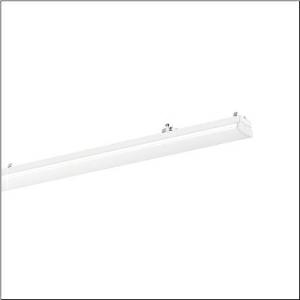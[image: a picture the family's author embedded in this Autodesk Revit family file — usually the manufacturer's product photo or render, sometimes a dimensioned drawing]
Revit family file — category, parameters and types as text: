
# Revit family: licross_r__21_recessed_opal_mo_52te1dvn465g_d803
name_source: partatom
category: Lighting Fixtures
units: mm (PartAtom-declared; Revit-internal decimal feet)

## family parameters
Cut with Voids When Loaded = No
Host = Face
Light Source = No
Part Type = Normal
Room Calculation Point = No
Round Connector Dimension = Use Diameter
Shared = No

## types (1)
- --- (1 x LED, 6500 lm, 37.7 W, 4000K)
    Apparent Load = 38 VA
    CIE Flux Codes = 44 73 91 87 100
    Color Rendering = 80
    Color Temperature = 4000K
    Default Elevation = 1800 mm
    Description = Licross® 21 recessed opal MO, luminaire insert, of sheet steel, galvanised, coil coated, white, length: 1.500mm, width: 66mm, height: 67mm, LED rated luminous flux: 6.500lm, light colour: 840, control gear: DALI 2, CLO, with plug, 5-pole, with phase selection, mains connection: 220..240V, AC, 50/60Hz, start of lifetime: 38W, end of service life: 45W, internal wiring halogen-free, primary optical cover: cover, of PMMA, light emission: direct with ceiling illumination distribution, primary light characteristic: symmetric, protection rating (complete): IP54, insulation class (complete): insulation class I (protective earthing), certification: CE, ENEC, VDE, UKCA, protection symbol: D if used in an environment with non-conductive dust loads with corresponding accessories, impact resistance: IK06, permissible ambient temperature for indoor applications: -25..+40°C, corresponds to IFS (International Featured Standards) requirements for safety and quality in the food industry, reducing of maximum allowable ambient temperature of 5°C with ceiling mounting, LABS conformity tested according to VDMA 24364:2018-05, packaging unit: 1 piece
    Height = 83 mm
    Lamp = 1 x LED
    Lamp Light Flux = 6500 lm
    Lamp Power = 37.7 W
    Lamp count = 1
    Length = 1500 mm
    Luminous efficacy = 172 lm/W
    Manufacturer = Siteco
    ModVariant = No
    Model = 52TE1DVN465G
    Mounting Place = Ceiling
    Mounting Type = Pendant
    Number of Poles = 1
    OnlyDefault = Yes
    Power Factor = 1
    Product Name = Licross® 21 recessed opal MO
    Product group = luminaire insert | ceiling pendant
    ProductGroupID = 902
    Protection Class = Protection class I
    Protection Degree = IP 54
    RLX_Detail_Level = 1
    RLX_Emergency_Light_Flux = 0 lm
    RLX_Emergency_Type = 0
    RLX_Emergency_Type_DB = No
    RlxData = <blob elided: 27321 chars, md5=6a89600c>
    Socket = socket
    Standby Power = 0 W
    System Light Flux = 6500 lm
    System Power = 38 W
    Type Comments = factory setting: luminous flux: 100 % | dim-lin: 254 | 252 mA
    Type Image = l_1313666.jpg
    URL = http://relux.com
    VarID = @adj_089761
    Voltage = 0 V
    Weight = 0.00 kg
    Width = 76 mm

## geometry (parser evidence)
native form markers: Blend x4, Sweep x14
no freeform markers — native parametric forms only
